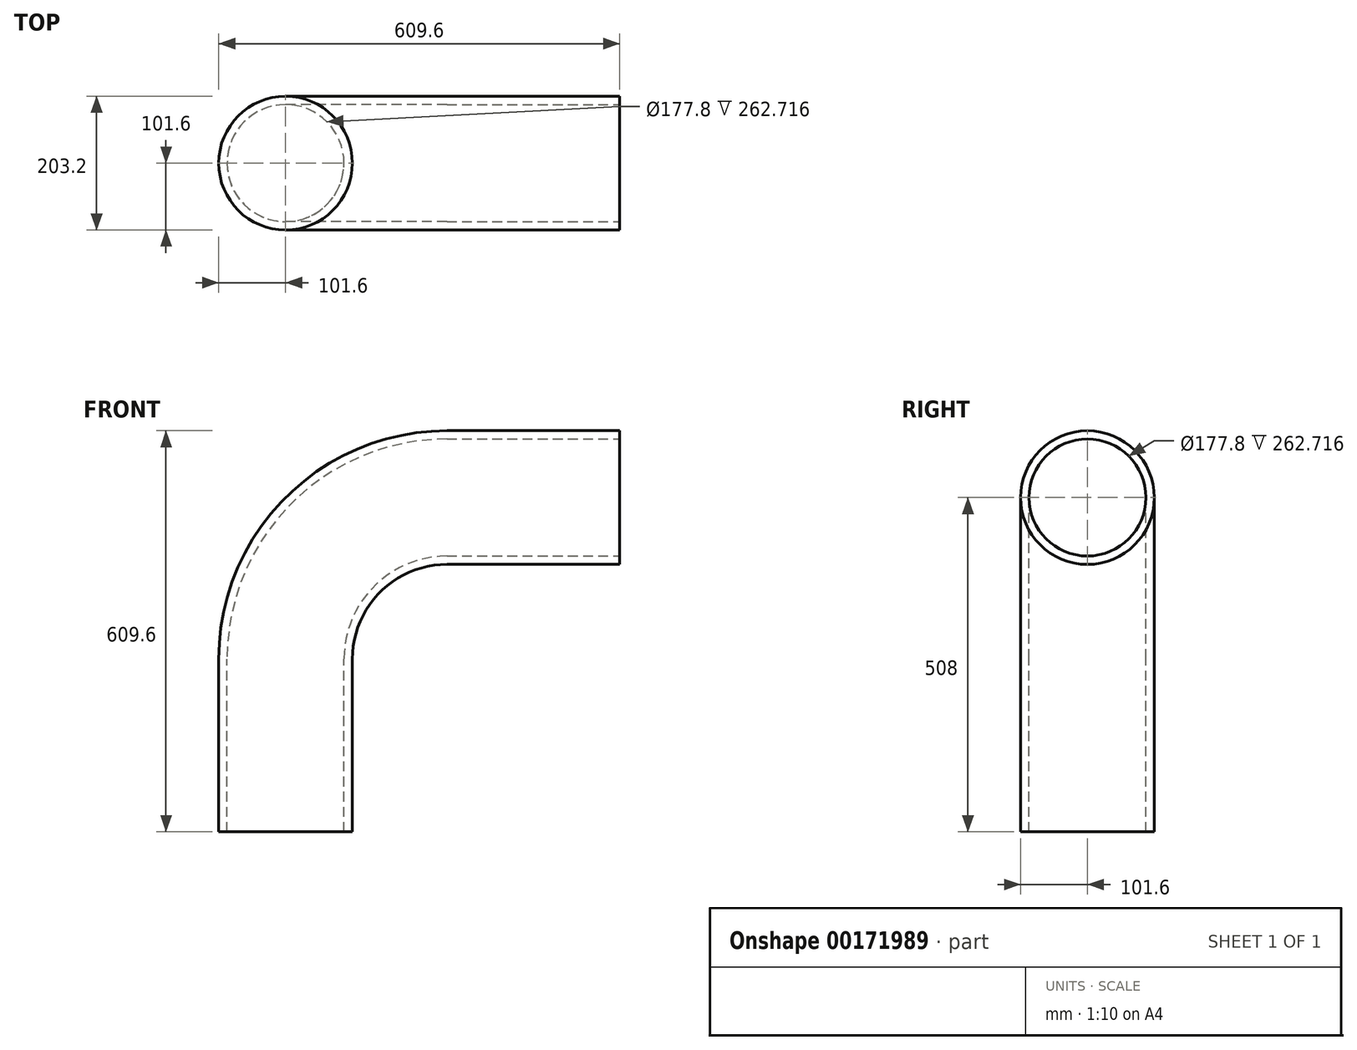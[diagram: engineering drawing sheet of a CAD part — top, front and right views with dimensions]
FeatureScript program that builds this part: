
annotation { "Feature Type Name" : "Feature", "Feature Type Description" : "" }
export const myFeature = defineFeature(function(context is Context, id is Id, definition is map)
    precondition{}
    {
        {
            var Q0;
            Q0=qCreatedBy(makeId("Front.planeOp"),FACE);
            var sketch = newSketch(context, id + "F0", { "sketchPlane" : qUnion([Q0])});
            skLineSegment(sketch, "E0.bottom", {"start": v(0, 0) * mm, "end": v(203.2, 0) * mm});
            skLineSegment(sketch, "E0.left", {"start": v(0, 0) * mm, "end": v(0, 262.72) * mm});
            skLineSegment(sketch, "E0.right", {"start": v(203.2, 0) * mm, "end": v(203.2, 262.72) * mm});
            skLineSegment(sketch, "E1.bottom", {"start": v(346.88, 609.6) * mm, "end": v(609.6, 609.6) * mm});
            skLineSegment(sketch, "E1.right", {"start": v(609.6, 609.6) * mm, "end": v(609.6, 406.4) * mm});
            skArc(sketch, "E2", {"start": v(346.88, 406.4) * mm, "mid": v(245.28, 364.32) * mm, "end": v(203.2, 262.72) * mm});
            skArc(sketch, "E3", {"start": v(346.88, 609.6) * mm, "mid": v(101.6, 508) * mm, "end": v(0, 262.72) * mm});
            skLineSegment(sketch, "E4.trimOffspring", {"start": v(346.88, 406.4) * mm, "end": v(609.6, 406.4) * mm});
            skSolve(sketch);
        }
        {
            var Q0;
            Q0=qSketchRegion(id+"F0",true);
            extrude(context, id + "F1", {"entities" : qUnion([Q0]), "depth" : 203.2 * mm});
        }
        {
            var Q0;
            Q0=makeQuery(id+"F1.opExtrude","CAP_EDGE",EDGE,{"disambiguationData":[OSD([sQuery(id+"F0.wireOp",EDGE,"E0.left")])],"isStart":false});
            var Q1;
            Q1=makeQuery(id+"F1.opExtrude","CAP_EDGE",EDGE,{"disambiguationData":[OSD([sQuery(id+"F0.wireOp",EDGE,"E0.right")])],"isStart":false});
            var Q2;
            Q2=makeQuery(id+"F1.opExtrude","CAP_EDGE",EDGE,{"disambiguationData":[OSD([sQuery(id+"F0.wireOp",EDGE,"E0.left")])],"isStart":true});
            var Q3;
            Q3=makeQuery(id+"F1.opExtrude","CAP_EDGE",EDGE,{"disambiguationData":[OSD([sQuery(id+"F0.wireOp",EDGE,"E0.right")])],"isStart":true});
            fillet(context, id + "F2", {"entities" : qUnion([Q0, Q1, Q2, Q3]), "radius" : 101.6 * mm, "tangentPropagation" : true, "allowEdgeOverflow" : false});
        }
        {
            var Q0;
            Q0=makeQuery(id+"F1.opExtrude","SWEPT_FACE",FACE,{"disambiguationData":[OSD([sQuery(id+"F0.wireOp",EDGE,"E0.bottom")])]});
            var Q1;
            Q1=makeQuery(id+"F1.opExtrude","SWEPT_FACE",FACE,{"disambiguationData":[OSD([sQuery(id+"F0.wireOp",EDGE,"E1.right")])]});
            shell(context, id + "F3", {"entities" : qUnion([Q0, Q1]), "thickness" : 12.7 * mm});
        }
    });
